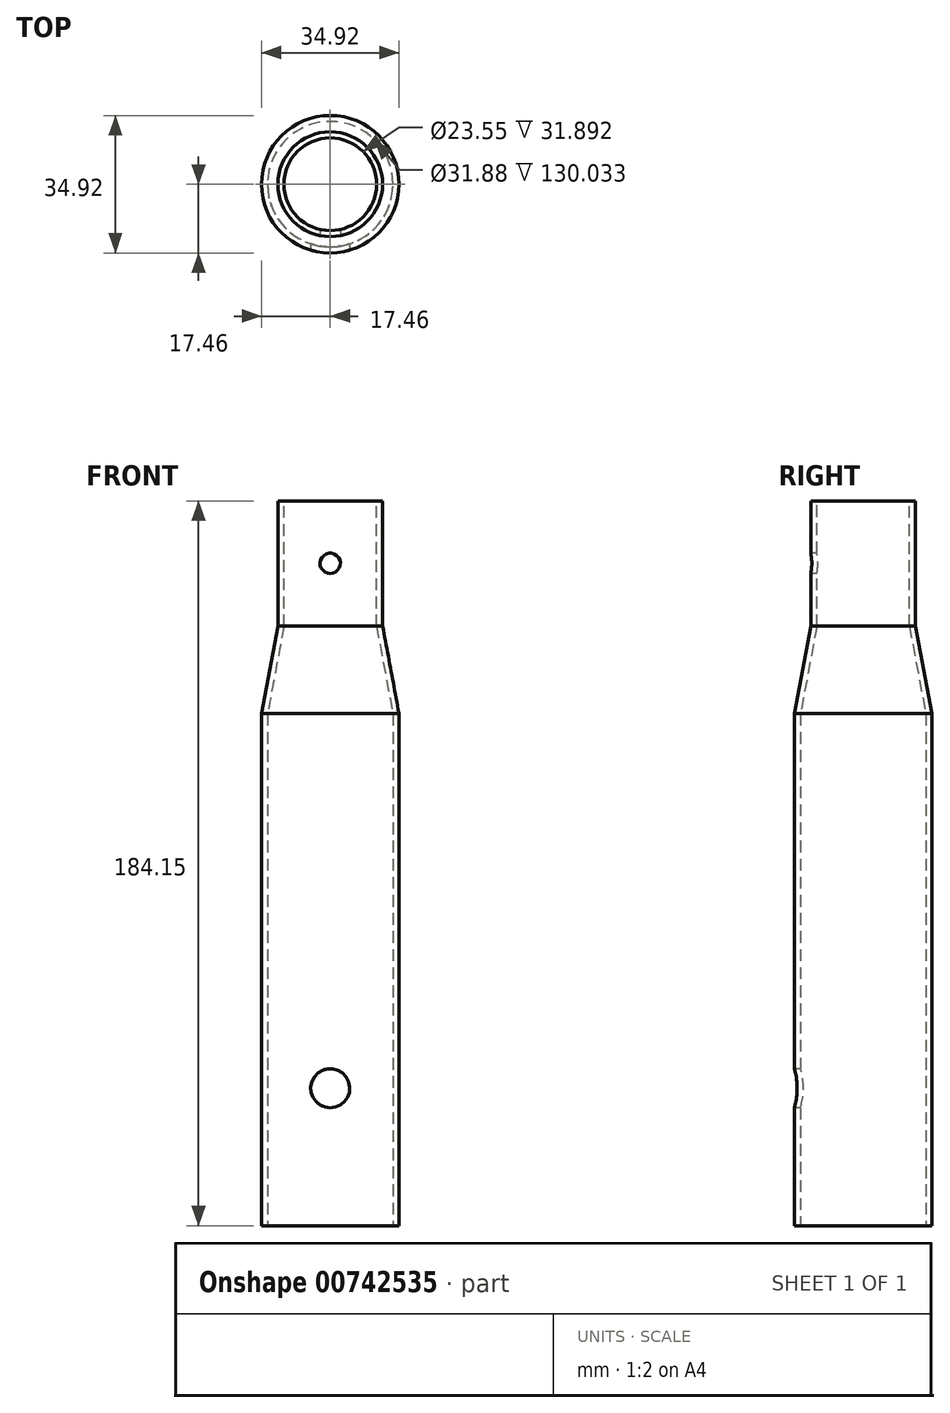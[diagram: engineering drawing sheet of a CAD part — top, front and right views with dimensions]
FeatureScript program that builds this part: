
annotation { "Feature Type Name" : "Feature", "Feature Type Description" : "" }
export const myFeature = defineFeature(function(context is Context, id is Id, definition is map)
    precondition{}
    {
        {
            var Q0;
            Q0=qCreatedBy(makeId("Top.planeOp"),FACE);
            var sketch = newSketch(context, id + "F0", { "sketchPlane" : qUnion([Q0])});
            skCircle(sketch, "E0", {"center": v(0, 0) * mm, "radius": 13.3 * mm});
            skSolve(sketch);
        }
        {
            var Q0;
            Q0=makeQuery(id+"F0.imprint","IMPRINT",FACE,{"disambiguationData":[TD([[makeQuery(id+"F0.imprint","IMPRINT",EDGE,{"derivedFrom":sQuery(id+"F0.wireOp",EDGE,"E0")}),1.0]])]});
            extrude(context, id + "F1", {"entities" : qUnion([Q0]), "oppositeDirection" : true, "depth" : 31.75 * mm, "offsetDistance" : 25.4 * mm});
        }
        {
            var Q0;
            Q0=qCreatedBy(makeId("Top.planeOp"),FACE);
            cPlane(context, id + "F2", {"entities" : qUnion([Q0]), "cplaneType" : CPlaneType.OFFSET, "offset" : 184.15 * mm, "oppositeDirection" : true, "width" : 152.4 * mm, "height" : 152.4 * mm});
        }
        {
            var Q0;
            Q0=qCreatedBy(id+"F2.planeOp",FACE);
            var sketch = newSketch(context, id + "F3", { "sketchPlane" : qUnion([Q0])});
            skCircle(sketch, "E1", {"center": v(0, 0) * mm, "radius": 17.46 * mm});
            skSolve(sketch);
        }
        {
            var Q0;
            Q0=makeQuery(id+"F3.imprint","IMPRINT",FACE,{"disambiguationData":[TD([[makeQuery(id+"F3.imprint","IMPRINT",EDGE,{"derivedFrom":sQuery(id+"F3.wireOp",EDGE,"E1")}),1.0]])]});
            extrude(context, id + "F4", {"entities" : qUnion([Q0]), "depth" : 130.17 * mm, "offsetDistance" : 25.4 * mm});
        }
        {
            var Q0;
            Q0=makeQuery(id+"F4.opExtrude","CAP_FACE",FACE,{"disambiguationData":[OSD([sQuery(id+"F3.wireOp",EDGE,"E1")])],"isStart":false});
            var Q1;
            Q1=makeQuery(id+"F1.opExtrude","CAP_FACE",FACE,{"disambiguationData":[OSD([sQuery(id+"F0.wireOp",EDGE,"E0")])],"isStart":false});
            loft(context, id + "F5", {"operationType" : NewBodyOperationType.ADD, "sheetProfilesArray" : [{ "sheetProfileEntities" : qUnion([Q0]) }, { "sheetProfileEntities" : qUnion([Q1]) }]});
        }
        {
            var Q0;
            Q0=makeQuery(id+"F1.opExtrude","CAP_FACE",FACE,{"disambiguationData":[OSD([sQuery(id+"F0.wireOp",EDGE,"E0")])],"isStart":true});
            var Q1;
            Q1=makeQuery(id+"F4.opExtrude","CAP_FACE",FACE,{"disambiguationData":[OSD([sQuery(id+"F3.wireOp",EDGE,"E1")])],"isStart":true});
            var Q2;
            Q2=makeQuery(id+"F1.opExtrude","SWEPT_BODY",BODY,{"disambiguationData":[OSD([sQuery(id+"F0.wireOp",EDGE,"E0")])]});
            shell(context, id + "F6", {"entities" : qUnion([Q0, Q1]), "parts" : qUnion([Q2]), "thickness" : 1.52 * mm});
        }
        {
            var Q0;
            Q0=qCreatedBy(makeId("Front.planeOp"),FACE);
            var sketch = newSketch(context, id + "F7", { "sketchPlane" : qUnion([Q0])});
            skPoint(sketch, "E2", {"position": v(0, -150.81) * mm});
            skPoint(sketch, "E3", {"position": v(0, -23.81) * mm});
            skPoint(sketch, "E4", {"position": v(0, 84.14) * mm});
            skSolve(sketch);
        }
        {
            var Q0;
            Q0=qCreatedBy(makeId("Front.planeOp"),FACE);
            cPlane(context, id + "F8", {"entities" : qUnion([Q0]), "cplaneType" : CPlaneType.OFFSET, "offset" : 17.46 * mm, "width" : 152.4 * mm, "height" : 152.4 * mm});
        }
        {
            var Q0;
            Q0=qCreatedBy(id+"F8.planeOp",FACE);
            var sketch = newSketch(context, id + "F9", { "sketchPlane" : qUnion([Q0])});
            skPoint(sketch, "E5", {"position": v(0, -149.22) * mm});
            skPoint(sketch, "E6", {"position": v(0, -23.81) * mm});
            skSolve(sketch);
        }
        {
            var Q0;
            Q0=qCreatedBy(makeId("Front.planeOp"),FACE);
            cPlane(context, id + "F10", {"entities" : qUnion([Q0]), "cplaneType" : CPlaneType.OFFSET, "offset" : 13.3 * mm, "width" : 152.4 * mm, "height" : 152.4 * mm});
        }
        {
            var Q0;
            Q0=qCreatedBy(id+"F10.planeOp",FACE);
            var sketch = newSketch(context, id + "F11", { "sketchPlane" : qUnion([Q0])});
            skPoint(sketch, "E7", {"position": v(0, -15.88) * mm});
            skSolve(sketch);
        }
        {
            var Q0;
            Q0=sQuery(id+"F9.wireOp",VERTEX,"E5");
            var Q1;
            Q1=makeQuery(id+"F1.opExtrude","SWEPT_BODY",BODY,{"disambiguationData":[OSD([sQuery(id+"F0.wireOp",EDGE,"E0")])]});
            hole(context, id + "F12", {"style" : HoleStyle.SIMPLE, "endStyle" : HoleEndStyle.BLIND, "holeDiameter" : 9.92 * mm, "majorDiameter" : 6.35 * mm, "holeDepth" : 6.35 * mm, "isTappedThrough" : true, "tappedDepth" : 12.7 * mm, "tapClearance" : 3, "startFromSketch" : true, "locations" : qUnion([Q0]), "scope" : qUnion([Q1])});
        }
        {
            var Q0;
            Q0=sQuery(id+"F11.wireOp",VERTEX,"E7");
            var Q1;
            Q1=makeQuery(id+"F1.opExtrude","SWEPT_BODY",BODY,{"disambiguationData":[OSD([sQuery(id+"F0.wireOp",EDGE,"E0")])]});
            hole(context, id + "F13", {"style" : HoleStyle.SIMPLE, "endStyle" : HoleEndStyle.BLIND, "holeDiameter" : 5.16 * mm, "majorDiameter" : 6.35 * mm, "holeDepth" : 6.35 * mm, "isTappedThrough" : true, "tappedDepth" : 12.7 * mm, "tapClearance" : 3, "startFromSketch" : true, "locations" : qUnion([Q0]), "scope" : qUnion([Q1])});
        }
    });
